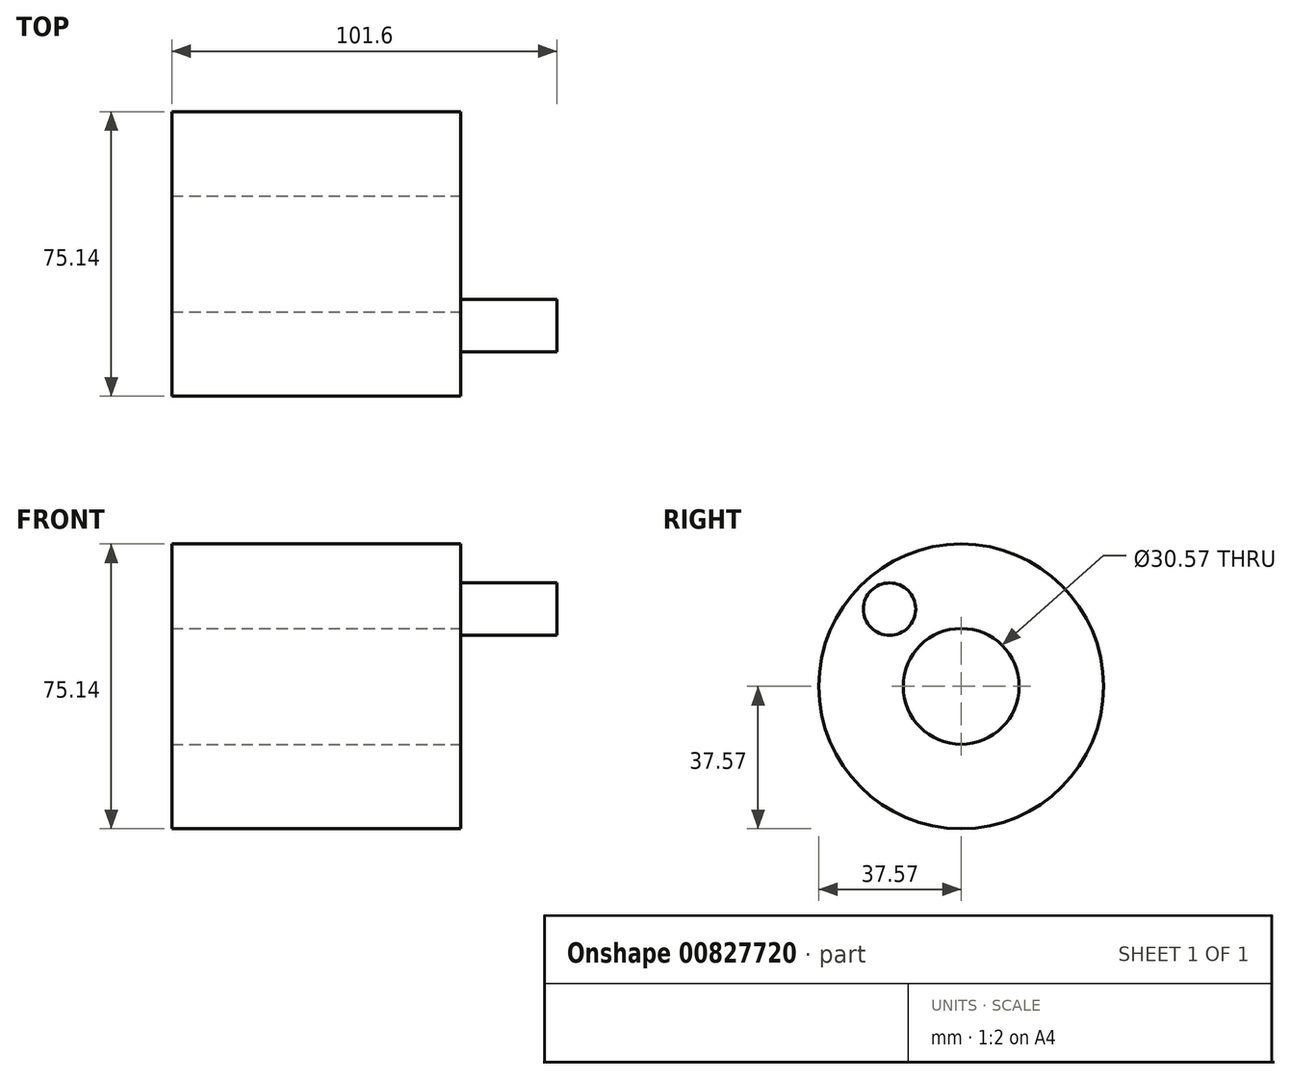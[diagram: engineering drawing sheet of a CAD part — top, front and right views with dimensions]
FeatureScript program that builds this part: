
annotation { "Feature Type Name" : "Feature", "Feature Type Description" : "" }
export const myFeature = defineFeature(function(context is Context, id is Id, definition is map)
    precondition{}
    {
        {
            var Q0;
            Q0=qCreatedBy(makeId("Right.planeOp"),FACE);
            var sketch = newSketch(context, id + "F0", { "sketchPlane" : qUnion([Q0])});
            skCircle(sketch, "E0", {"center": v(0, 0) * mm, "radius": 37.57 * mm});
            skPoint(sketch, "E1", {"position": v(-65.75, 40.25) * mm});
            skPoint(sketch, "E2", {"position": v(61.97, -41.09) * mm});
            skSolve(sketch);
        }
        {
            var Q0;
            Q0 = qSketchRegion(id + "F0", true);
            extrude(context, id + "F1", {"entities" : qUnion([Q0]), "depth" : 76.2 * mm, "offsetDistance" : 25.4 * mm});
        }
        {
            var Q0;
            Q0=makeQuery(id+"F1.opExtrude","CAP_FACE",FACE,{"disambiguationData":[OSD([sQuery(id+"F0.wireOp",EDGE,"E0")])],"isStart":false});
            var sketch = newSketch(context, id + "F2", { "sketchPlane" : qUnion([Q0])});
            skCircle(sketch, "E3", {"center": v(0, 0) * mm, "radius": 15.28 * mm});
            skSolve(sketch);
        }
        {
            var Q0;
            Q0 = qSketchRegion(id + "F2", true);
            extrude(context, id + "F3", {"entities" : qUnion([Q0]), "operationType" : NewBodyOperationType.REMOVE, "oppositeDirection" : true, "depth" : 76.2 * mm, "offsetDistance" : 25.4 * mm});
        }
        {
            var Q0;
            Q0=makeQuery(id+"F1.opExtrude","CAP_FACE",FACE,{"disambiguationData":[OSD([sQuery(id+"F0.wireOp",EDGE,"E0")])],"isStart":false});
            var sketch = newSketch(context, id + "F4", { "sketchPlane" : qUnion([Q0])});
            skCircle(sketch, "E4", {"center": v(-18.9, 20.4) * mm, "radius": 6.9 * mm});
            skSolve(sketch);
        }
        {
            var Q0;
            Q0 = qSketchRegion(id + "F4", true);
            extrude(context, id + "F5", {"entities" : qUnion([Q0]), "operationType" : NewBodyOperationType.ADD, "depth" : 25.4 * mm, "offsetDistance" : 25.4 * mm});
        }
    });
